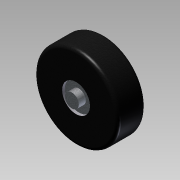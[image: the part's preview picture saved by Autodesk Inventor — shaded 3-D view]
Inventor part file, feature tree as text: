
AUTODESK INVENTOR PART (.ipt)
format: ipt  version: 2013 (Build 170138000, 138)  size: 142,848 bytes
history: native  units: in
note: dims shown in document units (in); Inventor stores cm internally (conversion verified against a paired STEP export)
features: extrude x5, sketch x5, fillet x1
ambient origin geometry x8: Origin, YZ Plane, XZ Plane, XY Plane, X Axis, Y Axis, Z Axis, Center Point
bodies: Solid1 (feature_tree)
feature tree (11):
  extrude  "Extrusion1"  Depth=1.0in TaperAngle=0.0deg
  extrude  "Extrusion2"  Depth=0.1in TaperAngle=0.0deg
  extrude  "Extrusion3"  Depth=0.1in TaperAngle=0.0deg
  fillet  "Fillet1"  Radius=0.125in
  extrude  "Extrusion4"  Depth=0.25in TaperAngle=0.0deg
  extrude  "Extrusion5"  Depth=0.25in TaperAngle=0.0deg
  sketch  "Sketch1"  dims[d0=3.0in d1=1.0in d2=0.0in]
  sketch  "Sketch2"  dims[d3=1.0in d4=0.1in d5=0.0in]
  sketch  "Sketch3"  dims[d6=1.0in d7=0.1in d8=0.0in d9=0.125in]
  sketch  "Sketch4"  dims[d10=0.5in d11=0.25in d12=0.0in]
  sketch  "Sketch5"  dims[d13=0.5in d14=0.25in d15=0.0in]
